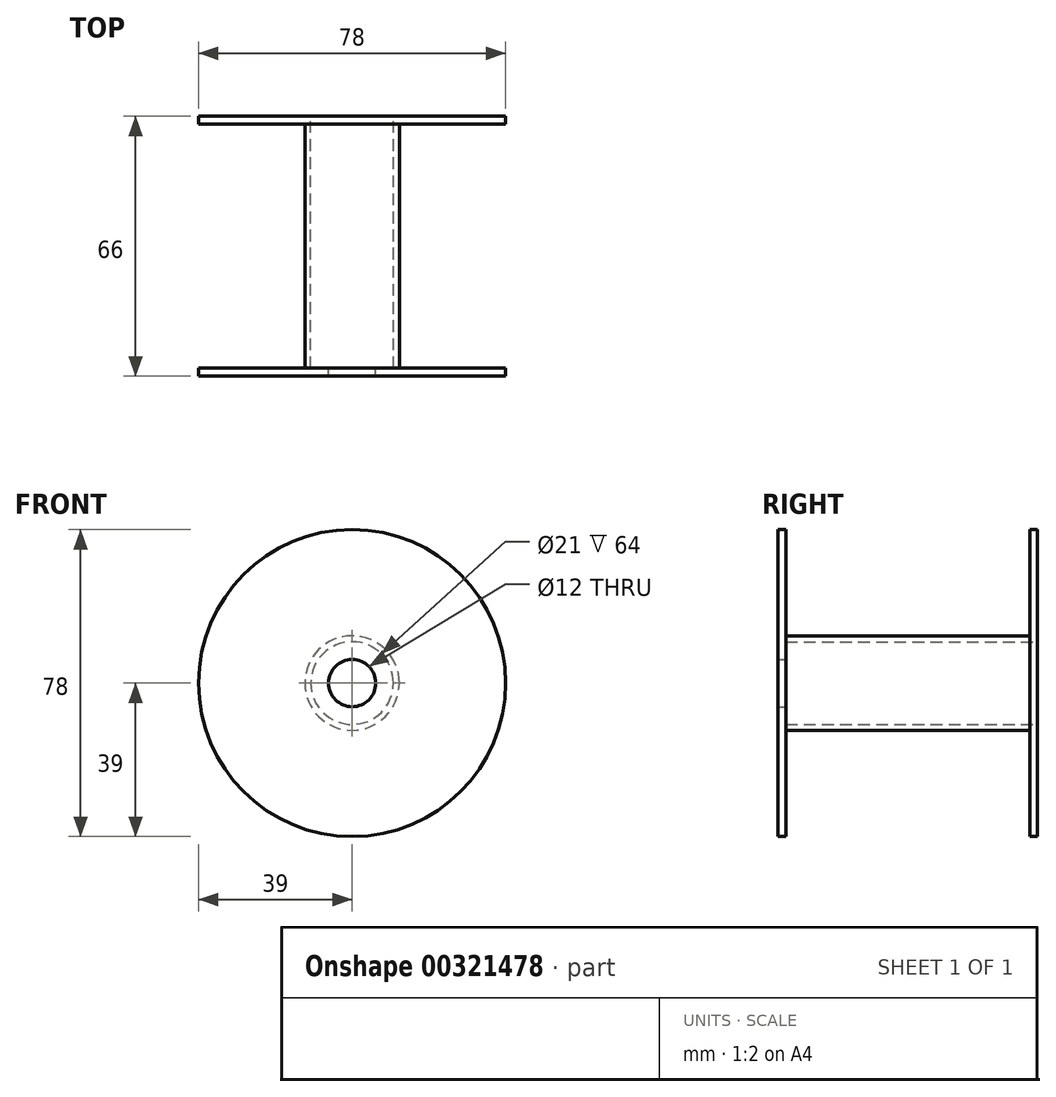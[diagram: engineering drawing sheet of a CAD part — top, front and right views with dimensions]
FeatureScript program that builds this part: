
annotation { "Feature Type Name" : "Feature", "Feature Type Description" : "" }
export const myFeature = defineFeature(function(context is Context, id is Id, definition is map)
    precondition{}
    {
        {
            var Q0;
            Q0=qCreatedBy(makeId("Front.planeOp"),FACE);
            var sketch = newSketch(context, id + "F0", { "sketchPlane" : qUnion([Q0])});
            skCircle(sketch, "E0", {"center": v(0, 0) * mm, "radius": 39 * mm});
            skCircle(sketch, "E1", {"center": v(0, 0) * mm, "radius": 10.5 * mm});
            skSolve(sketch);
        }
        {
            var Q0;
            Q0=qSketchRegion(id+"F0",true);
            extrude(context, id + "F1", {"entities" : qUnion([Q0]), "depth" : 2 * mm});
        }
        {
            var Q0;
            Q0=makeQuery(id+"F1.opExtrude","CAP_FACE",FACE,{"disambiguationData":[OSD([sQuery(id+"F0.wireOp",EDGE,"E0"),sQuery(id+"F0.wireOp",EDGE,"E1")])],"isStart":false});
            var sketch = newSketch(context, id + "F2", { "sketchPlane" : qUnion([Q0])});
            skCircle(sketch, "E2", {"center": v(0, 0) * mm, "radius": 10.5 * mm});
            skCircle(sketch, "E3", {"center": v(0, 0) * mm, "radius": 12 * mm});
            skSolve(sketch);
        }
        {
            var Q0;
            Q0=qSketchRegion(id+"F2",true);
            extrude(context, id + "F3", {"entities" : qUnion([Q0]), "operationType" : NewBodyOperationType.ADD, "depth" : 62 * mm});
        }
        {
            var Q0;
            Q0=makeQuery(id+"F3.opExtrude","CAP_FACE",FACE,{"disambiguationData":[OSD([sQuery(id+"F2.wireOp",EDGE,"E2"),sQuery(id+"F2.wireOp",EDGE,"E3")])],"isStart":false});
            var sketch = newSketch(context, id + "F4", { "sketchPlane" : qUnion([Q0])});
            skCircle(sketch, "E4", {"center": v(0, 0) * mm, "radius": 39 * mm});
            skCircle(sketch, "E5", {"center": v(0, 0) * mm, "radius": 6 * mm});
            skSolve(sketch);
        }
        {
            var Q0;
            Q0=qSketchRegion(id+"F4",true);
            extrude(context, id + "F5", {"entities" : qUnion([Q0]), "operationType" : NewBodyOperationType.ADD, "depth" : 2 * mm});
        }
    });
